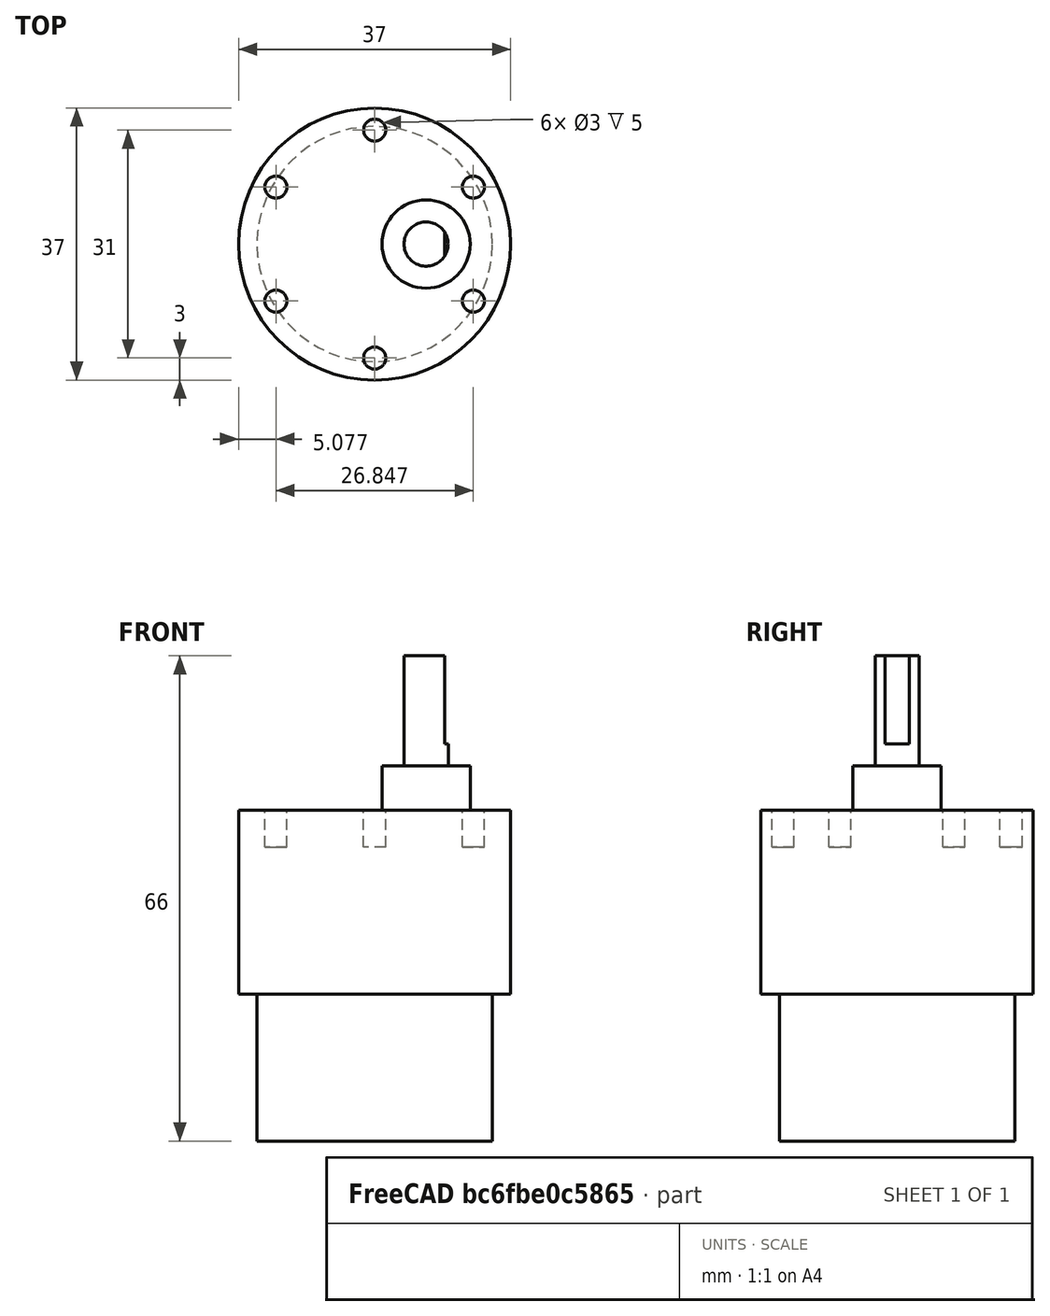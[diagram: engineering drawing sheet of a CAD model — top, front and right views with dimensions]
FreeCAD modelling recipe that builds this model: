
FCSTD DOCUMENT  (FreeCAD 0.17R13522 (Git))
Label: DC_Gear_Motor_37mm
License: All rights reserved
LicenseURL: http://en.wikipedia.org/wiki/All_rights_reserved
objects: Part::Cylinder×5, Part::MultiFuse×2, Part::Box×1, Part::FeaturePython×1, Part::Cut×1
note: 10 computed .brp shape members not serialized (recipe doc carries the construction recipe); baked Part::Feature solids carry a one-line shape summary decoded from their .brp

FEATURE [Part::Cylinder] Cylinder  label="Motor"
  Angle = 360
  AttacherType = Attacher::AttachEngine3D
  Height = 20
  Placement = pos=(0,0,-45) rot=(0,0,1;0rad)
  Radius = 16
FEATURE [Part::Cylinder] Cylinder001  label="Gear Box"
  Angle = 360
  AttacherType = Attacher::AttachEngine3D
  Height = 25
  Placement = pos=(0,0,-25) rot=(0,0,1;0rad)
  Radius = 18.5
FEATURE [Part::Cylinder] Cylinder002  label="Shaft Flange"
  Angle = 360
  AttacherType = Attacher::AttachEngine3D
  Height = 6
  Placement = pos=(7,0,0) rot=(0,0,1;0rad)
  Radius = 6
FEATURE [Part::Cylinder] Cylinder003  label="Shaft"
  Angle = 360
  AttacherType = Attacher::AttachEngine3D
  Height = 15
  Placement = pos=(7,0,6) rot=(0,0,1;0rad)
  Radius = 3
FEATURE [Part::Box] Box  label="Shaft D Cut Out"
  AttacherType = Attacher::AttachEngine3D
  Height = 12
  Length = 10
  Placement = pos=(9.5,-5,9) rot=(0,0,1;0rad)
  Width = 10
FEATURE [Part::Cylinder] Cylinder004  label="Screw"
  Angle = 360
  AttacherType = Attacher::AttachEngine3D
  Height = 5
  Placement = pos=(0,-15.5,-5) rot=(0,0,1;0rad)
  Radius = 1.5
FEATURE [Part::FeaturePython] Array  label="Screw Array"  # Draft array (typed FeaturePython)
  Angle = 360
  ArrayType = 1
  Axis = (0,0,1)
  Base = -> Cylinder004
  Center = (0,0,0)
  Fuse = false
  IntervalAxis = (0,0,0)
  IntervalX = (1,0,0)
  IntervalY = (0,1,0)
  IntervalZ = (0,0,0)
  NumberPolar = 6
  NumberX = 1
  NumberY = 1
  NumberZ = 1
FEATURE [Part::MultiFuse] Fusion  label="Negative Fusion"
  Shapes = -> [Array,Box]
FEATURE [Part::MultiFuse] Fusion001  label="Positive Fusion"
  Shapes = -> [Cylinder,Cylinder001,Cylinder002,Cylinder003]
FEATURE [Part::Cut] Cut  label="DC Gear Motor 37mm"
  Base = -> Fusion001
  Tool = -> Fusion
